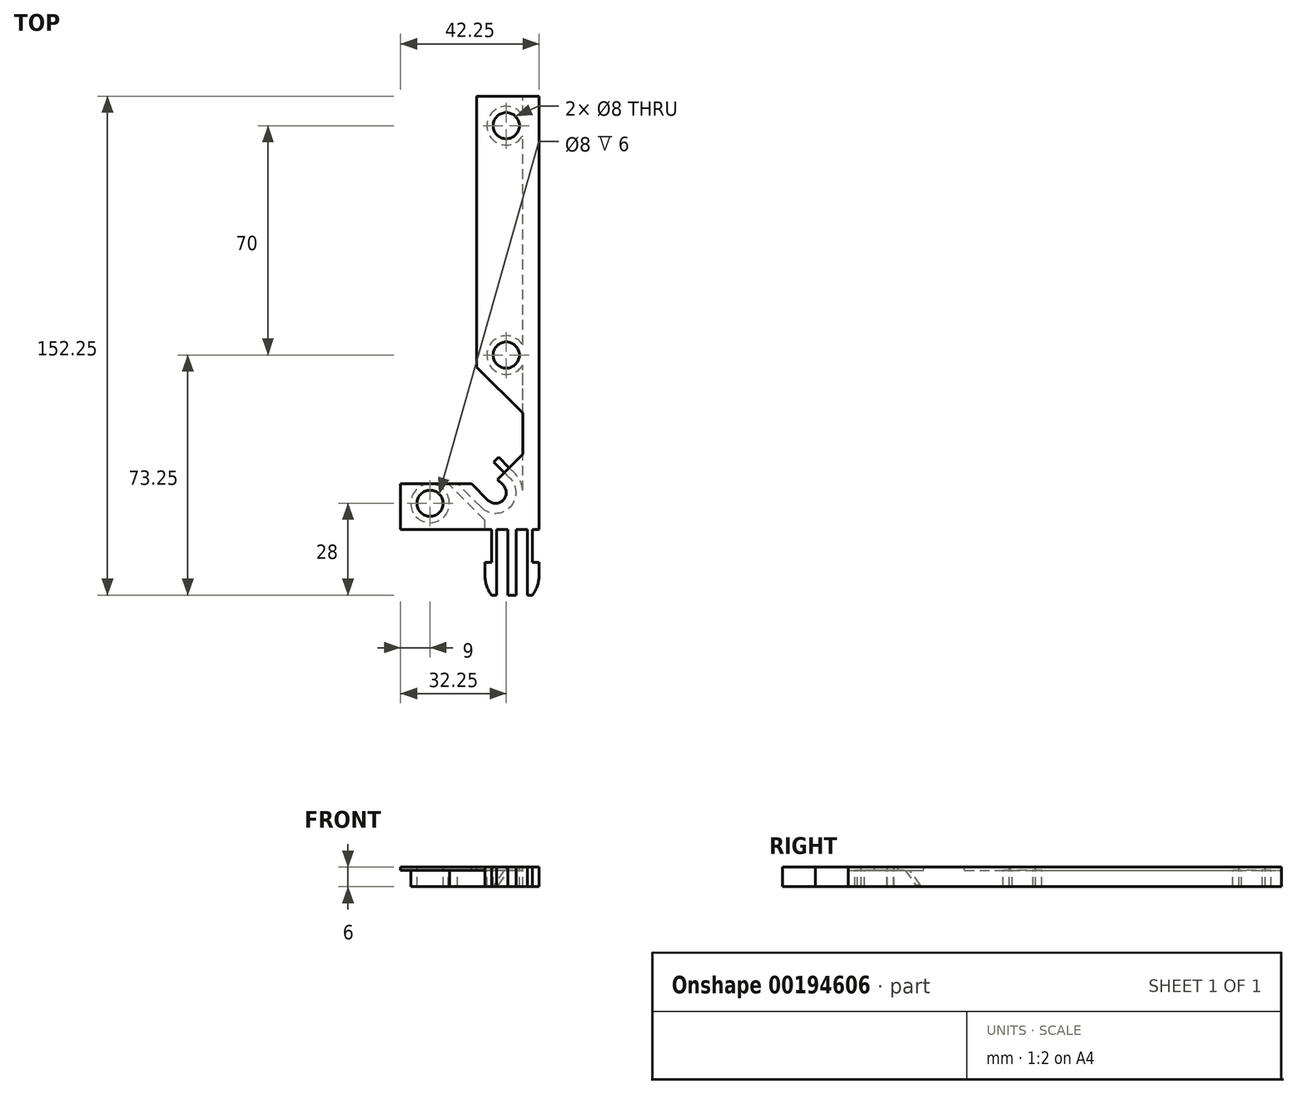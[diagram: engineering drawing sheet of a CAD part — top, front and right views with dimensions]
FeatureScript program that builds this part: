
annotation { "Feature Type Name" : "Feature", "Feature Type Description" : "" }
export const myFeature = defineFeature(function(context is Context, id is Id, definition is map)
    precondition{}
    {
        {
            var Q0;
            Q0=qCreatedBy(makeId("Top.planeOp"),FACE);
            var sketch = newSketch(context, id + "F0", { "sketchPlane" : qUnion([Q0])});
            skCircle(sketch, "E0", {"center": v(0, 0) * mm, "radius": 3.25 * mm});
            skCircle(sketch, "E1", {"center": v(-20, -3.25) * mm, "radius": 4 * mm});
            skCircle(sketch, "E2", {"center": v(3.25, 42) * mm, "radius": 4 * mm});
            skLineSegment(sketch, "E3", {"start": v(8.25, 24.27) * mm, "end": v(-5.75, 38.27) * mm});
            skLineSegment(sketch, "E4", {"start": v(-5.75, 38.27) * mm, "end": v(-5.75, 52) * mm});
            skLineSegment(sketch, "E5", {"start": v(13.25, 52) * mm, "end": v(-5.75, 52) * mm});
            skLineSegment(sketch, "E6", {"start": v(13.25, 52) * mm, "end": v(13.25, -11.25) * mm});
            skLineSegment(sketch, "E7", {"start": v(13.25, -11.25) * mm, "end": v(-29, -11.25) * mm});
            skLineSegment(sketch, "E8", {"start": v(-29, -11.25) * mm, "end": v(-29, 2.75) * mm});
            skLineSegment(sketch, "E9", {"start": v(-29, 2.75) * mm, "end": v(-7.35, 2.75) * mm});
            skLineSegment(sketch, "E10", {"start": v(-7.35, 2.75) * mm, "end": v(-2.3, -2.3) * mm});
            skLineSegment(sketch, "E11", {"start": v(2.3, 2.3) * mm, "end": v(0.53, 4.07) * mm});
            skLineSegment(sketch, "E12", {"start": v(0.53, 4.07) * mm, "end": v(8.25, 11.79) * mm});
            skLineSegment(sketch, "E13", {"start": v(8.25, 11.79) * mm, "end": v(8.25, 24.27) * mm});
            skCircle(sketch, "E14", {"center": v(3.25, 112) * mm, "radius": 4 * mm});
            skLineSegment(sketch, "E15", {"start": v(-5.75, 52) * mm, "end": v(-5.75, 121) * mm});
            skLineSegment(sketch, "E16", {"start": v(-5.75, 121) * mm, "end": v(13.25, 121) * mm});
            skLineSegment(sketch, "E17", {"start": v(13.25, 121) * mm, "end": v(13.25, 52) * mm});
            skSolve(sketch);
        }
        {
            var Q0;
            Q0=makeQuery(id+"F0.imprint","IMPRINT",FACE,{"disambiguationData":[TD([[makeQuery(id+"F0.imprint","IMPRINT",EDGE,{"derivedFrom":sQuery(id+"F0.wireOp",EDGE,"E1")}),-1.0]])]});
            var Q1;
            Q1=makeQuery(id+"F0.imprint","IMPRINT",FACE,{"disambiguationData":[TD([[makeQuery(id+"F0.imprint","IMPRINT",EDGE,{"derivedFrom":sQuery(id+"F0.wireOp",EDGE,"E5")}),-1.0]])]});
            extrude(context, id + "F1", {"entities" : qUnion([Q0, Q1]), "oppositeDirection" : true, "depth" : 1 * mm});
        }
        {
            var Q0;
            Q0=makeQuery(id+"F1.opExtrude","CAP_FACE",FACE,{"disambiguationData":[OSD([sQuery(id+"F0.wireOp",EDGE,"E0"),sQuery(id+"F0.wireOp",EDGE,"E1"),sQuery(id+"F0.wireOp",EDGE,"E2"),sQuery(id+"F0.wireOp",EDGE,"E3"),sQuery(id+"F0.wireOp",EDGE,"E4"),sQuery(id+"F0.wireOp",EDGE,"E5"),sQuery(id+"F0.wireOp",EDGE,"E6"),sQuery(id+"F0.wireOp",EDGE,"E7"),sQuery(id+"F0.wireOp",EDGE,"E8"),sQuery(id+"F0.wireOp",EDGE,"E9"),sQuery(id+"F0.wireOp",EDGE,"E10"),sQuery(id+"F0.wireOp",EDGE,"E11"),sQuery(id+"F0.wireOp",EDGE,"E12"),sQuery(id+"F0.wireOp",EDGE,"E13")])],"isStart":false});
            var sketch = newSketch(context, id + "F2", { "sketchPlane" : qUnion([Q0])});
            skCircle(sketch, "E18", {"center": v(0, 0) * mm, "radius": 6.25 * mm});
            skCircle(sketch, "E19", {"center": v(-20, 3.25) * mm, "radius": 5.9 * mm});
            skCircle(sketch, "E20", {"center": v(3.25, -42) * mm, "radius": 5.9 * mm});
            skLineSegment(sketch, "E21", {"start": v(-4.42, 4.42) * mm, "end": v(-11.59, -2.75) * mm});
            skLineSegment(sketch, "E22", {"start": v(4.42, -4.42) * mm, "end": v(2.65, -6.19) * mm});
            skCircle(sketch, "E23", {"center": v(0, 0) * mm, "radius": 8.28 * mm});
            skLineSegment(sketch, "E24", {"start": v(-5.85, 5.85) * mm, "end": v(-14.45, -2.75) * mm});
            skLineSegment(sketch, "E25", {"start": v(5.85, -5.85) * mm, "end": v(4.08, -7.62) * mm});
            skCircle(sketch, "E26", {"center": v(3.25, -112) * mm, "radius": 5.9 * mm});
            skSolve(sketch);
        }
        {
            var Q0;
            Q0=makeQuery(id+"F2.imprint","IMPRINT",FACE,{"disambiguationData":[TD([[makeQuery(id+"F2.imprint","IMPRINT",EDGE,{"derivedFrom":sQuery(id+"F2.wireOp",EDGE,"E19")}),1.0]])]});
            var Q1;
            {var subQ5=sQuery(id+"F2.wireOp",EDGE,"E24");Q1=makeQuery(id+"F2.imprint","IMPRINT",FACE,{"disambiguationData":[TD([[makeQuery(id+"F2.imprint","IMPRINT",EDGE,{"derivedFrom":subQ5}),1.0]])]});}
            var Q2;
            {var subQ7=sQuery(id+"F2.wireOp",EDGE,"E22");Q2=makeQuery(id+"F2.imprint","IMPRINT",FACE,{"disambiguationData":[TD([[makeQuery(id+"F2.imprint","IMPRINT",EDGE,{"derivedFrom":subQ7}),1.0]])]});}
            var Q3;
            {var subQ0=sQuery(id+"F2.wireOp",EDGE,"E25");Q3=makeQuery(id+"F2.imprint","IMPRINT",FACE,{"disambiguationData":[TD([[makeQuery(id+"F2.imprint","IMPRINT",EDGE,{"derivedFrom":subQ0}),-1.0]])]});}
            var Q4;
            Q4=makeQuery(id+"F2.imprint","IMPRINT",FACE,{"disambiguationData":[TD([[makeQuery(id+"F2.imprint","IMPRINT",EDGE,{"derivedFrom":sQuery(id+"F2.wireOp",EDGE,"E20")}),1.0]])]});
            var Q5;
            Q5=makeQuery(id+"F2.imprint","IMPRINT",FACE,{"disambiguationData":[TD([[makeQuery(id+"F2.imprint","IMPRINT",EDGE,{"derivedFrom":sQuery(id+"F2.wireOp",EDGE,"E26")}),1.0]])]});
            extrude(context, id + "F3", {"entities" : qUnion([Q0, Q1, Q2, Q3, Q4, Q5]), "operationType" : NewBodyOperationType.ADD, "depth" : 5 * mm});
        }
        {
            var Q0;
            Q0=makeQuery(id+"F3.opExtrude","SWEPT_FACE",FACE,{"disambiguationData":[OSD([sQuery(id+"F2.wireOp",EDGE,"E25")])]});
            var sketch = newSketch(context, id + "F4", { "sketchPlane" : qUnion([Q0])});
            skLineSegment(sketch, "E27", {"start": v(2.5, -6) * mm, "end": v(7, -6) * mm});
            skLineSegment(sketch, "E28", {"start": v(7, -6) * mm, "end": v(7, -5.5) * mm});
            skLineSegment(sketch, "E29", {"start": v(7, -5.5) * mm, "end": v(2.5, -1) * mm});
            skLineSegment(sketch, "E30", {"start": v(2.5, -1) * mm, "end": v(2.5, -6) * mm});
            skSolve(sketch);
        }
        {
            var Q0;
            Q0=qSketchRegion(id+"F4",true);
            var Q1;
            Q1=makeQuery(id+"F3.opExtrude","SWEPT_FACE",FACE,{"disambiguationData":[OSD([sQuery(id+"F2.wireOp",EDGE,"E22")])]});
            extrude(context, id + "F5", {"entities" : qUnion([Q0]), "operationType" : NewBodyOperationType.ADD, "endBound" : BoundingType.UP_TO_SURFACE, "oppositeDirection" : true, "endBoundEntityFace" : qUnion([Q1]), "depth" : 25 * mm});
        }
        {
            var Q0;
            {var subQ0=sQuery(id+"F0.wireOp",EDGE,"E16");var subQ1=sQuery(id+"F0.wireOp",EDGE,"E8");var subQ2=sQuery(id+"F0.wireOp",EDGE,"E12");var subQ3=sQuery(id+"F0.wireOp",EDGE,"E9");var subQ4=sQuery(id+"F0.wireOp",EDGE,"E3");var subQ5=sQuery(id+"F0.wireOp",EDGE,"E15");var subQ6=sQuery(id+"F0.wireOp",EDGE,"E4");var subQ7=sQuery(id+"F0.wireOp",EDGE,"E13");var subQ8=sQuery(id+"F0.wireOp",EDGE,"E17");var subQ9=sQuery(id+"F0.wireOp",EDGE,"E6");var subQ10=sQuery(id+"F0.wireOp",EDGE,"E7");Q0=makeQuery(id+"F3.boolean.opBoolean","SPLIT",FACE,{"disambiguationData":[TD([makeQuery(id+"F1.opExtrude","SWEPT_FACE",FACE,{"disambiguationData":[OSD([subQ4])]})])],"derivedFrom":makeQuery(id+"F1.opExtrude","CAP_FACE",FACE,{"disambiguationData":[OSD([sQuery(id+"F0.wireOp",EDGE,"E0"),sQuery(id+"F0.wireOp",EDGE,"E1"),sQuery(id+"F0.wireOp",EDGE,"E2"),subQ4,subQ6,subQ9,subQ10,subQ1,subQ3,sQuery(id+"F0.wireOp",EDGE,"E10"),sQuery(id+"F0.wireOp",EDGE,"E11"),subQ2,subQ7,sQuery(id+"F0.wireOp",EDGE,"E14"),subQ5,subQ0,subQ8])],"isStart":false})});}
            var sketch = newSketch(context, id + "F6", { "sketchPlane" : qUnion([Q0])});
            skLineSegment(sketch, "E31.bottom", {"start": v(13.25, 11.25) * mm, "end": v(8.25, 11.25) * mm});
            skLineSegment(sketch, "E31.top", {"start": v(13.25, -121) * mm, "end": v(8.25, -121) * mm});
            skLineSegment(sketch, "E31.left", {"start": v(13.25, 11.25) * mm, "end": v(13.25, -121) * mm});
            skLineSegment(sketch, "E31.right", {"start": v(8.25, 11.25) * mm, "end": v(8.25, -121) * mm});
            skSolve(sketch);
        }
        {
            var Q0;
            Q0=qSketchRegion(id+"F6",true);
            extrude(context, id + "F7", {"entities" : qUnion([Q0]), "operationType" : NewBodyOperationType.ADD, "depth" : 5 * mm});
        }
        {
            var Q0;
            Q0=qCreatedBy(makeId("Top.planeOp"),FACE);
            var sketch = newSketch(context, id + "F8", { "sketchPlane" : qUnion([Q0])});
            skLineSegment(sketch, "E32", {"start": v(13.25, -11.25) * mm, "end": v(-3.25, -11.25) * mm});
            skLineSegment(sketch, "E33", {"start": v(9.75, -11.25) * mm, "end": v(9.75, -31.25) * mm});
            skLineSegment(sketch, "E34", {"start": v(0.25, -11.25) * mm, "end": v(0.25, -31.25) * mm});
            skLineSegment(sketch, "E35", {"start": v(6.25, -11.25) * mm, "end": v(6.25, -31.25) * mm});
            skLineSegment(sketch, "E36", {"start": v(6.25, -31.25) * mm, "end": v(3.75, -31.25) * mm});
            skLineSegment(sketch, "E37", {"start": v(3.75, -31.25) * mm, "end": v(3.75, -11.25) * mm});
            skLineSegment(sketch, "E38", {"start": v(9.75, -31.25) * mm, "end": v(11.25, -31.25) * mm});
            skLineSegment(sketch, "E39", {"start": v(0.25, -31.25) * mm, "end": v(-1.25, -31.25) * mm});
            skLineSegment(sketch, "E40", {"start": v(11.25, -11.25) * mm, "end": v(11.25, -21.25) * mm});
            skLineSegment(sketch, "E41", {"start": v(11.25, -21.25) * mm, "end": v(13.25, -21.25) * mm});
            skLineSegment(sketch, "E42", {"start": v(-1.25, -11.25) * mm, "end": v(-1.25, -21.25) * mm});
            skLineSegment(sketch, "E43", {"start": v(-1.25, -21.25) * mm, "end": v(-3.25, -21.25) * mm});
            skLineSegment(sketch, "E44", {"start": v(-3.25, -21.25) * mm, "end": v(-3.25, -25.25) * mm});
            skLineSegment(sketch, "E45", {"start": v(13.25, -21.25) * mm, "end": v(13.25, -25.25) * mm});
            skArc(sketch, "E46", {"start": v(11.25, -31.25) * mm, "mid": v(12.74, -28.41) * mm, "end": v(13.25, -25.25) * mm});
            skLineSegment(sketch, "E47", {"start": v(5, -11.25) * mm, "end": v(5, -31.25) * mm, "construction": true});
            skArc(sketch, "E48.MirrorCS", {"start": v(-1.25, -31.25) * mm, "mid": v(-2.74, -28.41) * mm, "end": v(-3.25, -25.25) * mm});
            skLineSegment(sketch, "E49.top", {"start": v(13.25, -6.25) * mm, "end": v(-3.25, -6.25) * mm});
            skLineSegment(sketch, "E49.left", {"start": v(13.25, -11.25) * mm, "end": v(13.25, -6.25) * mm});
            skLineSegment(sketch, "E49.right", {"start": v(-3.25, -11.25) * mm, "end": v(-3.25, -6.25) * mm});
            skArc(sketch, "E50", {"start": v(5.42, -6.25) * mm, "mid": v(7.53, -3.43) * mm, "end": v(8.28, 0) * mm});
            skLineSegment(sketch, "E51", {"start": v(8.28, 0) * mm, "end": v(13.25, 0) * mm});
            skLineSegment(sketch, "E52", {"start": v(13.25, 0) * mm, "end": v(13.25, -6.25) * mm});
            skLineSegment(sketch, "E53", {"start": v(-3.25, -8.45) * mm, "end": v(-5.85, -5.85) * mm});
            skLineSegment(sketch, "E54", {"start": v(-5.85, -5.85) * mm, "end": v(-3.25, -6.25) * mm});
            skSolve(sketch);
        }
        {
            var Q0;
            Q0=qSketchRegion(id+"F8",true);
            extrude(context, id + "F9", {"entities" : qUnion([Q0]), "operationType" : NewBodyOperationType.ADD, "oppositeDirection" : true, "depth" : 6 * mm});
        }
    });
